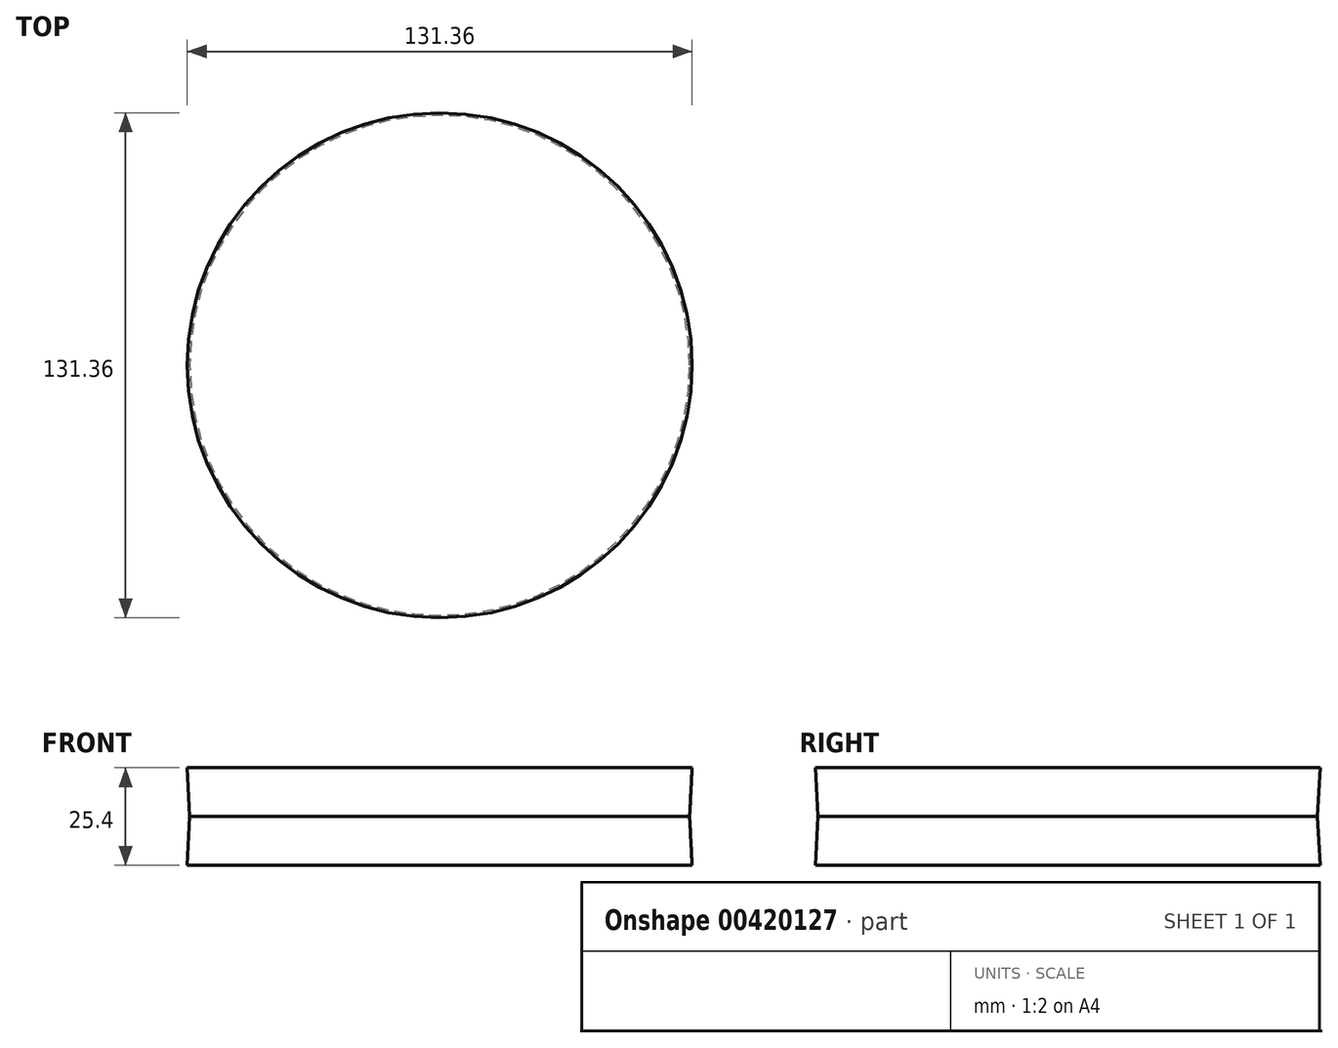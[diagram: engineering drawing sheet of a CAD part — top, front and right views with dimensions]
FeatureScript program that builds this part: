
annotation { "Feature Type Name" : "Feature", "Feature Type Description" : "" }
export const myFeature = defineFeature(function(context is Context, id is Id, definition is map)
    precondition{}
    {
        {
            var Q0;
            Q0=qCreatedBy(makeId("Top.planeOp"),FACE);
            var sketch = newSketch(context, id + "F0", { "sketchPlane" : qUnion([Q0])});
            skCircle(sketch, "E0", {"center": v(0, 0) * mm, "radius": 65 * mm});
            skSolve(sketch);
        }
        {
            var Q0;
            Q0=makeQuery(id+"F0.imprint","IMPRINT",FACE,{"disambiguationData":[TD([[makeQuery(id+"F0.imprint","IMPRINT",EDGE,{"derivedFrom":sQuery(id+"F0.wireOp",EDGE,"E0")}),1.0]])]});
            extrude(context, id + "F1", {"entities" : qUnion([Q0]), "endBound" : BoundingType.SYMMETRIC, "depth" : 25.4 * mm, "hasDraft" : true, "draftAngle" : 3 * degree});
        }
    });
